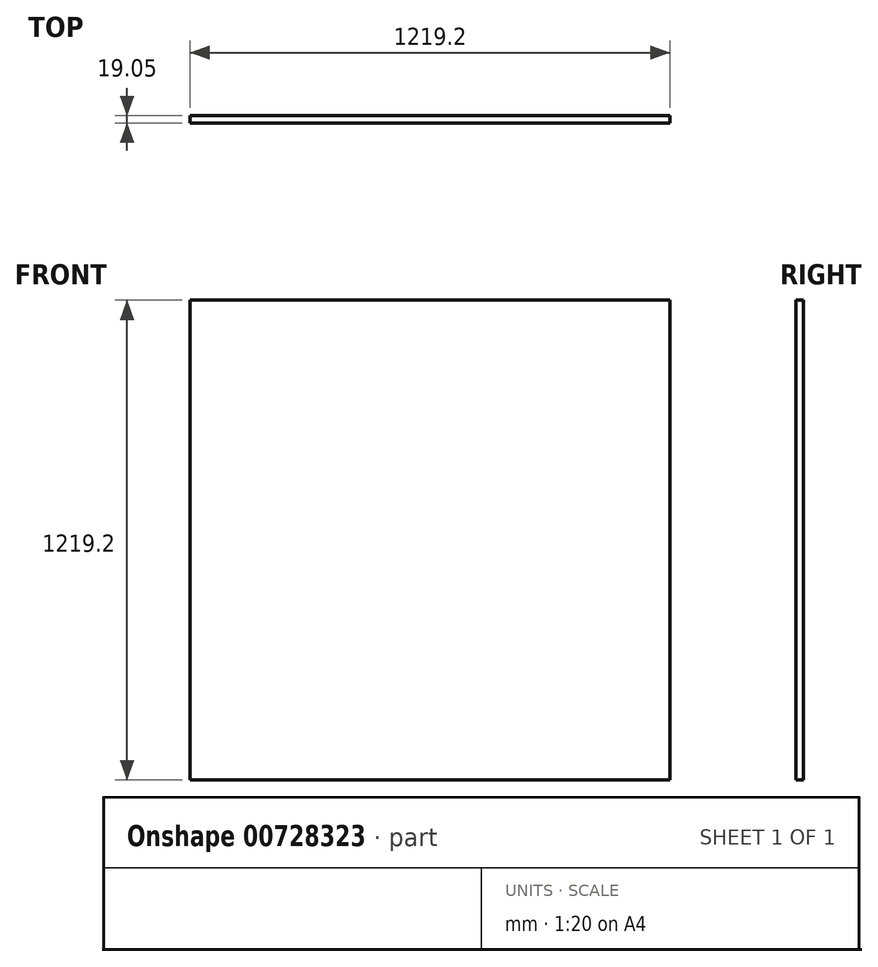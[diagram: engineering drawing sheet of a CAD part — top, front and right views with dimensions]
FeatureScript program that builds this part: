
annotation { "Feature Type Name" : "Feature", "Feature Type Description" : "" }
export const myFeature = defineFeature(function(context is Context, id is Id, definition is map)
    precondition{}
    {
        {
            var Q0;
            Q0=qCreatedBy(makeId("Front.planeOp"),FACE);
            var sketch = newSketch(context, id + "F0", { "sketchPlane" : qUnion([Q0])});
            skLineSegment(sketch, "E0.bottom", {"start": v(-609.6, -609.6) * mm, "end": v(609.6, -609.6) * mm});
            skLineSegment(sketch, "E0.top", {"start": v(-609.6, 609.6) * mm, "end": v(609.6, 609.6) * mm});
            skLineSegment(sketch, "E0.left", {"start": v(-609.6, -609.6) * mm, "end": v(-609.6, 609.6) * mm});
            skLineSegment(sketch, "E0.right", {"start": v(609.6, -609.6) * mm, "end": v(609.6, 609.6) * mm});
            skPoint(sketch, "E0.middle", {"position": v(0, 0) * mm});
            skSolve(sketch);
        }
        {
            var Q0;
            Q0=qSketchRegion(id+"F0",true);
            extrude(context, id + "F1", {"entities" : qUnion([Q0]), "depth" : 19.05 * mm});
        }
    });
